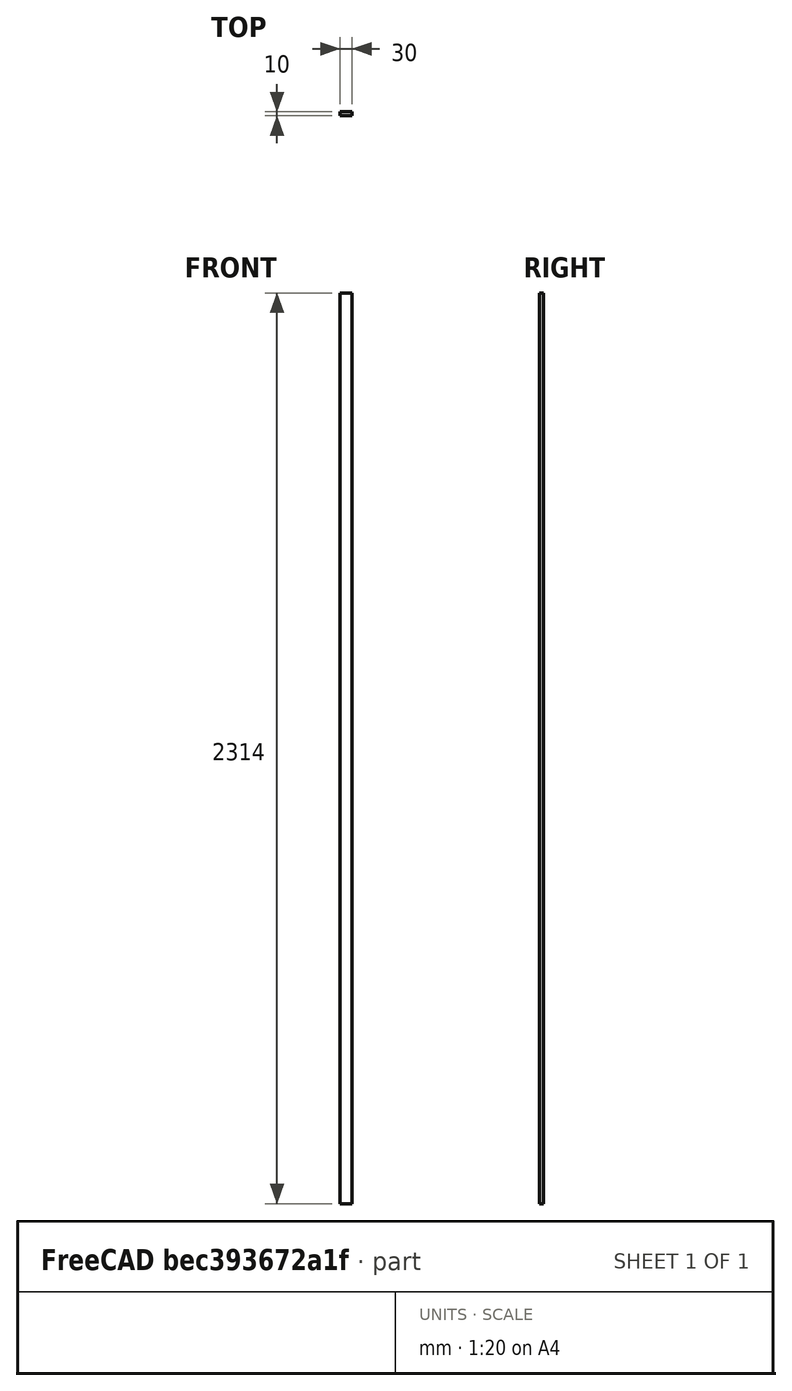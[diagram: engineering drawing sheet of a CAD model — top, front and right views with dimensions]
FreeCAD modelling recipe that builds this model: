
FCSTD DOCUMENT  (FreeCAD 0.21R33771 (Git))
Label: reflector_2024_listello
License: All rights reserved
LicenseURL: https://en.wikipedia.org/wiki/All_rights_reserved
objects: Spreadsheet::Sheet×1, Sketcher::SketchObject×1, PartDesign::Pad×1, PartDesign::Body×1
note: 4 computed .brp shape members not serialized (recipe doc carries the construction recipe); baked Part::Feature solids carry a one-line shape summary decoded from their .brp

FEATURE [Spreadsheet::Sheet] Spreadsheet  label="d"
  cells = A1='width; B1(width)=30; A2='height; B2(height)=10; A3='length; B3(length)==2440 - 63 - 63
FEATURE [Sketcher::SketchObject] Sketch
  FullyConstrained = true
  MapMode = 5
  Support = -> [XY_Plane]
  expr: Constraints[8] = <<d>>.width
  expr: Constraints[9] = <<d>>.height
  sketch-geometry (4):
    g0: LineSegment StartX=-15 StartY=5 StartZ=0 EndX=15 EndY=5 EndZ=0
    g1: LineSegment StartX=15 StartY=5 StartZ=0 EndX=15 EndY=-5 EndZ=0
    g2: LineSegment StartX=15 StartY=-5 StartZ=0 EndX=-15 EndY=-5 EndZ=0
    g3: LineSegment StartX=-15 StartY=-5 StartZ=0 EndX=-15 EndY=5 EndZ=0
  constraints (10):
    c: Coincident(g0,g1)
    c: Coincident(g1,g2)
    c: Coincident(g2,g3)
    c: Coincident(g3,g0)
    c: Horizontal(g2)
    c: Vertical(g3)
    c: Symmetric(g0,g0,g-2)
    c: Symmetric(g0,g1,g-1)
    c: DistanceX(g0,g0) = 30
    c: DistanceY(g1,g1) = 10
FEATURE [PartDesign::Pad] Pad
  Direction = (0,0,1)
  Length = 2314
  Length2 = 10
  Midplane = true
  Profile = -> Sketch
  ReferenceAxis = -> Sketch [N_Axis]
  Type = 0
  expr: Length = <<d>>.length
FEATURE [PartDesign::Body] Body
  Group = -> [Sketch,Pad]
  Origin = -> Origin
  Tip = -> Pad
